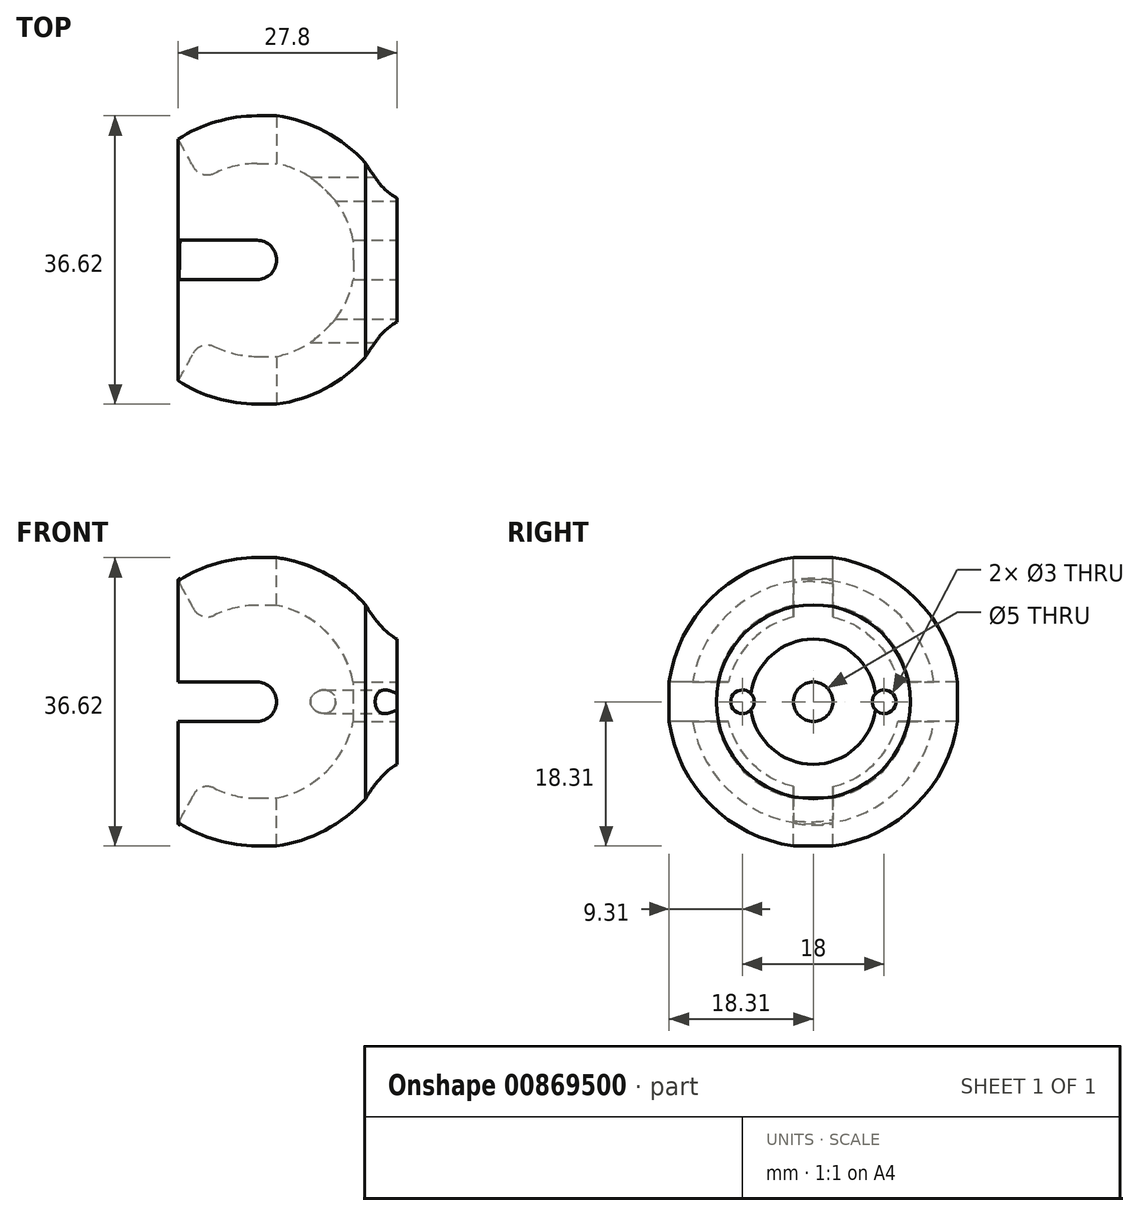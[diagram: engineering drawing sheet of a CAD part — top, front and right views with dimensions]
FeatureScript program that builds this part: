
annotation { "Feature Type Name" : "Feature", "Feature Type Description" : "" }
export const myFeature = defineFeature(function(context is Context, id is Id, definition is map)
    precondition{}
    {
        {
            var Q0;
            Q0=qCreatedBy(makeId("Front.planeOp"),FACE);
            var sketch = newSketch(context, id + "F0", { "sketchPlane" : qUnion([Q0])});
            skLineSegment(sketch, "E0", {"start": v(12.5, 0) * mm, "end": v(57.5, 0) * mm});
            skArc(sketch, "E1", {"start": v(12.46, 0.95) * mm, "mid": v(5.4, 11.27) * mm, "end": v(-7.07, 10.3) * mm});
            skFitSpline(sketch, "E2", {"points": [v(13.78, 12.32) * mm, v(24.8, 6.77) * mm, v(61.3, 8.08) * mm], "startDerivative": vector(27.08, -44.66) * mm, "endDerivative": vector(62.99, 8.12) * mm});
            skLineSegment(sketch, "E3", {"start": v(12.46, 0.95) * mm, "end": v(17.8, 0.95) * mm});
            skPoint(sketch, "E4.end.orphan", {"position": v(82.25, 0.95) * mm});
            skPoint(sketch, "E5.orphan", {"position": v(82.5, -1.55) * mm});
            skArc(sketch, "E6", {"start": v(13.78, 12.32) * mm, "mid": v(2.48, 18.32) * mm, "end": v(-10, 15.54) * mm});
            skLineSegment(sketch, "E7", {"start": v(-7.07, 10.3) * mm, "end": v(-10, 15.54) * mm});
            skLineSegment(sketch, "E8", {"start": v(17.8, 7.95) * mm, "end": v(17.8, 0.95) * mm});
            skPoint(sketch, "E9.start.orphan", {"position": v(74.25, 0.95) * mm});
            skSolve(sketch);
        }
        {
            var Q0;
            Q0=makeQuery(id+"F0.imprint","IMPRINT",FACE,{"disambiguationData":[TD([[makeQuery(id+"F0.imprint","IMPRINT",EDGE,{"derivedFrom":sQuery(id+"F0.wireOp",EDGE,"E1")}),-1.0]])]});
            var Q1;
            Q1=sQuery(id+"F0.wireOp",EDGE,"E0");
            revolve(context, id + "F1", {"entities" : qUnion([Q0]), "axis" : qUnion([Q1]), "revolveType" : RevolveType.FULL});
        }
        {
            var Q0;
            Q0=makeQuery(id+"F1.opRevolve","SWEPT_EDGE",EDGE,{"disambiguationData":[OSD([sQuery(id+"F0.wireOp",EDGE,"E1"),sQuery(id+"F0.wireOp",EDGE,"CbFEBDJi-CplH-pibZ-NPAv-z09MQRNn6UNR")])]});
            var Q1;
            Q1=makeQuery(id+"F1.opRevolve","SWEPT_EDGE",EDGE,{"disambiguationData":[OSD([sQuery(id+"F0.wireOp",EDGE,"E9"),sQuery(id+"F0.wireOp",EDGE,"8ef04d3b-c97b-4cb2-96d4-a3e5af4470d5.trimOffspring")])]});
            fillet(context, id + "F2", {"entities" : qUnion([Q0, Q1]), "radius" : 2 * mm, "tangentPropagation" : true, "allowEdgeOverflow" : false});
        }
        {
            var Q0;
            Q0=makeQuery(id+"F1.opRevolve","SWEPT_FACE",FACE,{"disambiguationData":[OSD([sQuery(id+"F0.wireOp",EDGE,"E8")])]});
            var sketch = newSketch(context, id + "F3", { "sketchPlane" : qUnion([Q0])});
            skCircle(sketch, "E10", {"center": v(-9, 0) * mm, "radius": 1.5 * mm});
            skCircle(sketch, "E11", {"center": v(9, 0) * mm, "radius": 1.5 * mm});
            skCircle(sketch, "E12", {"center": v(0, 0) * mm, "radius": 2.5 * mm});
            skSolve(sketch);
        }
        {
            var Q0;
            {var subQ0=sQuery(id+"F3.wireOp",EDGE,"E10");var subQ1=makeQuery(id+"F1.opRevolve","SWEPT_EDGE",EDGE,{"disambiguationData":[OSD([sQuery(id+"F0.wireOp",EDGE,"E2"),sQuery(id+"F0.wireOp",EDGE,"E8")])]});var subQ2=makeQuery(id+"F3.imprint","INTERSECT",VERTEX,{"disambiguationData":[OD(0.0)],"derivedFrom":[subQ1,subQ0]});Q0=makeQuery(id+"F3.imprint","IMPRINT",FACE,{"disambiguationData":[TD([[makeQuery(id+"F3.imprint","IMPRINT",EDGE,{"disambiguationData":[TD([[subQ2,-1.0]])],"derivedFrom":subQ0}),1.0]])]});}
            var Q1;
            {var subQ0=sQuery(id+"F3.wireOp",EDGE,"E11");var subQ1=makeQuery(id+"F1.opRevolve","SWEPT_EDGE",EDGE,{"disambiguationData":[OSD([sQuery(id+"F0.wireOp",EDGE,"E2"),sQuery(id+"F0.wireOp",EDGE,"E8")])]});var subQ2=makeQuery(id+"F3.imprint","INTERSECT",VERTEX,{"disambiguationData":[OD(0.0)],"derivedFrom":[subQ1,subQ0]});Q1=makeQuery(id+"F3.imprint","IMPRINT",FACE,{"disambiguationData":[TD([[makeQuery(id+"F3.imprint","IMPRINT",EDGE,{"disambiguationData":[TD([[subQ2,-1.0]])],"derivedFrom":subQ0}),1.0]])]});}
            var Q2;
            {var subQ0=sQuery(id+"F3.wireOp",EDGE,"E11");var subQ1=makeQuery(id+"F1.opRevolve","SWEPT_EDGE",EDGE,{"disambiguationData":[OSD([sQuery(id+"F0.wireOp",EDGE,"E2"),sQuery(id+"F0.wireOp",EDGE,"E8")])]});var subQ2=makeQuery(id+"F3.imprint","INTERSECT",VERTEX,{"disambiguationData":[OD(0.0)],"derivedFrom":[subQ1,subQ0]});Q2=makeQuery(id+"F3.imprint","IMPRINT",FACE,{"disambiguationData":[TD([[makeQuery(id+"F3.imprint","IMPRINT",EDGE,{"disambiguationData":[TD([[subQ2,1.0]])],"derivedFrom":subQ0}),1.0]])]});}
            var Q3;
            {var subQ0=sQuery(id+"F3.wireOp",EDGE,"E10");var subQ1=makeQuery(id+"F1.opRevolve","SWEPT_EDGE",EDGE,{"disambiguationData":[OSD([sQuery(id+"F0.wireOp",EDGE,"E2"),sQuery(id+"F0.wireOp",EDGE,"E8")])]});var subQ2=makeQuery(id+"F3.imprint","INTERSECT",VERTEX,{"disambiguationData":[OD(0.0)],"derivedFrom":[subQ1,subQ0]});Q3=makeQuery(id+"F3.imprint","IMPRINT",FACE,{"disambiguationData":[TD([[makeQuery(id+"F3.imprint","IMPRINT",EDGE,{"disambiguationData":[TD([[subQ2,1.0]])],"derivedFrom":subQ0}),1.0]])]});}
            extrude(context, id + "F4", {"entities" : qUnion([Q0, Q1, Q2, Q3]), "operationType" : NewBodyOperationType.REMOVE, "endBound" : BoundingType.THROUGH_ALL, "oppositeDirection" : true, "depth" : 25 * mm});
        }
        {
            var Q0;
            Q0=qSketchRegion(id+"F3",true);
            extrude(context, id + "F5", {"entities" : qUnion([Q0]), "operationType" : NewBodyOperationType.REMOVE, "endBound" : BoundingType.THROUGH_ALL, "oppositeDirection" : true, "depth" : 25 * mm});
        }
        {
            var Q0;
            Q0=qCreatedBy(makeId("Front.planeOp"),FACE);
            var sketch = newSketch(context, id + "F6", { "sketchPlane" : qUnion([Q0])});
            skArc(sketch, "E13", {"start": v(0, -2.5) * mm, "mid": v(2.5, 0) * mm, "end": v(0, 2.5) * mm});
            skLineSegment(sketch, "E14", {"start": v(0, 2.5) * mm, "end": v(-10.11, 2.5) * mm});
            skLineSegment(sketch, "E15", {"start": v(0, -2.5) * mm, "end": v(-10.11, -2.5) * mm});
            skLineSegment(sketch, "E16", {"start": v(-10.11, -2.5) * mm, "end": v(-10.11, 2.5) * mm});
            skSolve(sketch);
        }
        {
            var Q0;
            Q0=qSketchRegion(id+"F6",true);
            extrude(context, id + "F7", {"entities" : qUnion([Q0]), "operationType" : NewBodyOperationType.REMOVE, "endBound" : BoundingType.SYMMETRIC, "oppositeDirection" : true, "depth" : 50 * mm});
        }
        {
            var Q0;
            Q0=qCreatedBy(makeId("Top.planeOp"),FACE);
            var sketch = newSketch(context, id + "F8", { "sketchPlane" : qUnion([Q0])});
            skArc(sketch, "E17", {"start": v(0, -2.5) * mm, "mid": v(2.5, 0) * mm, "end": v(0, 2.5) * mm});
            skLineSegment(sketch, "E18", {"start": v(0, 2.5) * mm, "end": v(-9.79, 2.5) * mm});
            skLineSegment(sketch, "E19", {"start": v(0, -2.5) * mm, "end": v(-9.88, -2.5) * mm});
            skLineSegment(sketch, "E20", {"start": v(-9.88, -2.5) * mm, "end": v(-9.79, 2.5) * mm});
            skSolve(sketch);
        }
        {
            var Q0;
            Q0=qSketchRegion(id+"F8",true);
            extrude(context, id + "F9", {"entities" : qUnion([Q0]), "operationType" : NewBodyOperationType.REMOVE, "endBound" : BoundingType.SYMMETRIC, "oppositeDirection" : true, "depth" : 50 * mm});
        }
    });
